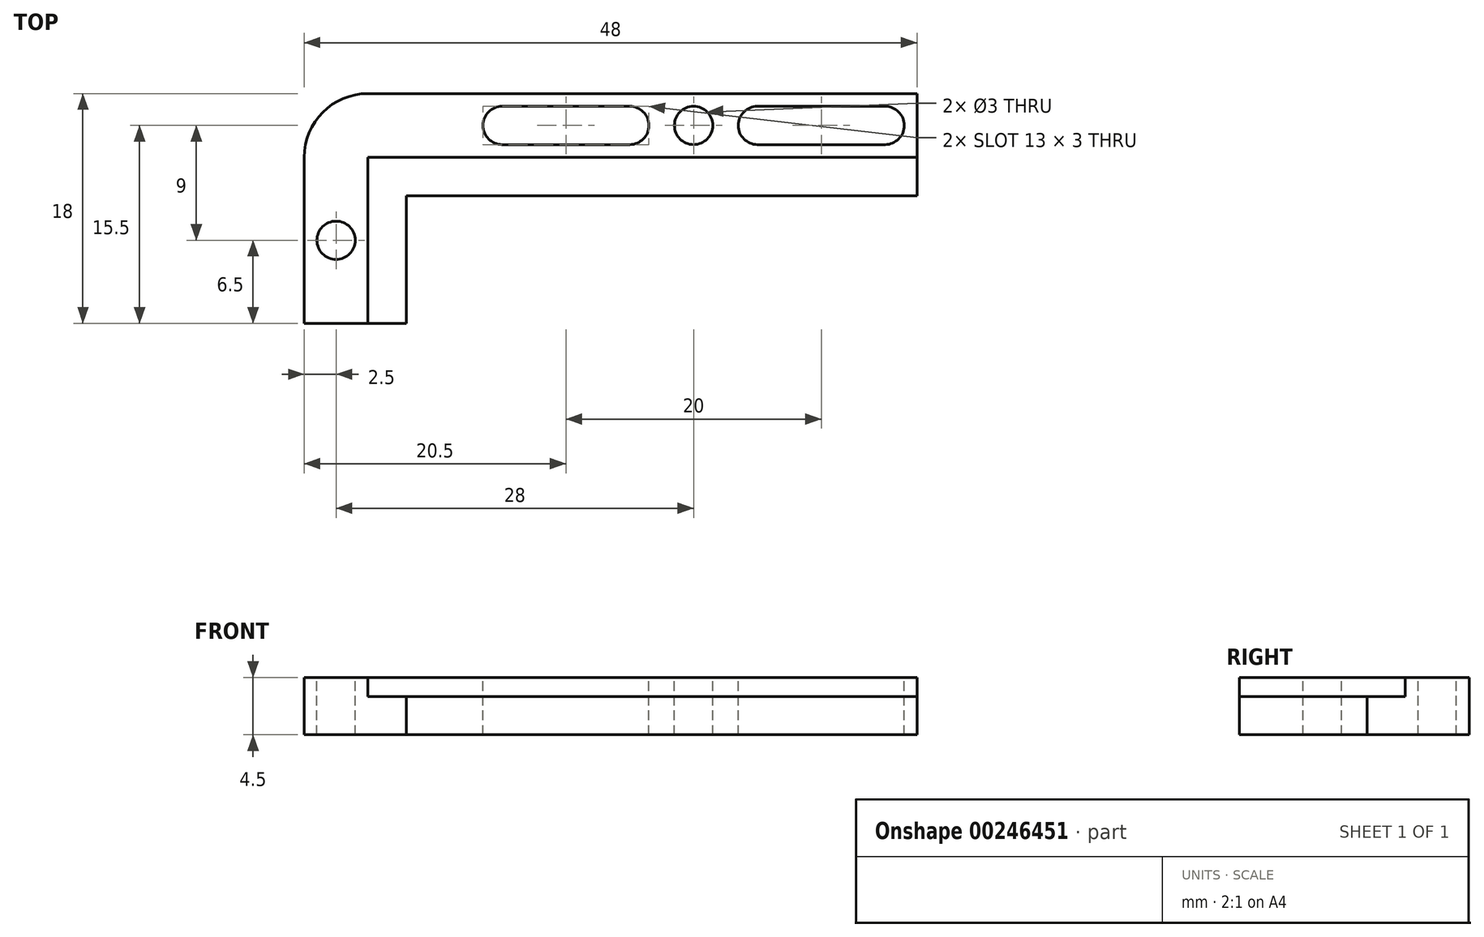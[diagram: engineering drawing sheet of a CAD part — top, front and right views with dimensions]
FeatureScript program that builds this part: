
annotation { "Feature Type Name" : "Feature", "Feature Type Description" : "" }
export const myFeature = defineFeature(function(context is Context, id is Id, definition is map)
    precondition{}
    {
        {
            assignVariable(context, id + "F0", {"name" : "pcb_thickness", "anyValue" : 1.5});
        }
        {
            assignVariable(context, id + "F1", {"name" : "clamp_thickness", "anyValue" : 3});
        }
        {
            assignVariable(context, id + "F2", {"name" : "clamp_depth", "anyValue" : 5});
        }
        {
            var Q0;
            Q0=qCreatedBy(makeId("Top.planeOp"),FACE);
            var sketch = newSketch(context, id + "F3", { "sketchPlane" : qUnion([Q0])});
            skLineSegment(sketch, "E0", {"start": v(0, 0) * mm, "end": v(40, 0) * mm});
            skLineSegment(sketch, "E1", {"start": v(40, 0) * mm, "end": v(40, 8) * mm});
            skLineSegment(sketch, "E2", {"start": v(40, 8) * mm, "end": v(-8, 8) * mm});
            skLineSegment(sketch, "E3", {"start": v(-8, 8) * mm, "end": v(-8, -10) * mm});
            skLineSegment(sketch, "E4", {"start": v(-8, -10) * mm, "end": v(0, -10) * mm});
            skLineSegment(sketch, "E5", {"start": v(0, -10) * mm, "end": v(0, 0) * mm});
            skSolve(sketch);
        }
        {
            var Q0;
            Q0 = qSketchRegion(id + "F3", true);
            extrude(context, id + "F4", {"entities" : qUnion([Q0]), "depth" : (getVariable(context, 'clamp_thickness') + getVariable(context, 'pcb_thickness')) * mm});
        }
        {
            var Q0;
            Q0=makeQuery(id+"F4.opExtrude","SWEPT_FACE",FACE,{"disambiguationData":[OSD([sQuery(id+"F3.wireOp",EDGE,"E1")])]});
            var sketch = newSketch(context, id + "F5", { "sketchPlane" : qUnion([Q0])});
            skLineSegment(sketch, "E6.bottom", {"start": v(0, 4.5) * mm, "end": v(3, 4.5) * mm});
            skLineSegment(sketch, "E6.top", {"start": v(0, 3) * mm, "end": v(3, 3) * mm});
            skLineSegment(sketch, "E6.left", {"start": v(0, 4.5) * mm, "end": v(0, 3) * mm});
            skLineSegment(sketch, "E6.right", {"start": v(3, 4.5) * mm, "end": v(3, 3) * mm});
            skSolve(sketch);
        }
        {
            var Q0;
            Q0=makeQuery(id+"F5.imprint","IMPRINT",FACE,{"disambiguationData":[TD([[makeQuery(id+"F5.imprint","IMPRINT",EDGE,{"derivedFrom":sQuery(id+"F5.wireOp",EDGE,"E6.bottom")}),-1.0]])]});
            var Q1;
            Q1=makeQuery(id+"F4.opExtrude","CAP_EDGE",EDGE,{"disambiguationData":[OSD([sQuery(id+"F3.wireOp",EDGE,"E0")])],"isStart":false});
            var Q2;
            Q2=makeQuery(id+"F4.opExtrude","CAP_EDGE",EDGE,{"disambiguationData":[OSD([sQuery(id+"F3.wireOp",EDGE,"E5")])],"isStart":false});
            sweep(context, id + "F6", {"operationType" : NewBodyOperationType.REMOVE, "profiles" : qUnion([Q0]), "path" : qUnion([Q1, Q2])});
        }
        {
            var Q0;
            Q0=makeQuery(id+"F4.opExtrude","CAP_FACE",FACE,{"disambiguationData":[OSD([sQuery(id+"F3.wireOp",EDGE,"E0"),sQuery(id+"F3.wireOp",EDGE,"E1"),sQuery(id+"F3.wireOp",EDGE,"E2"),sQuery(id+"F3.wireOp",EDGE,"E3"),sQuery(id+"F3.wireOp",EDGE,"E4"),sQuery(id+"F3.wireOp",EDGE,"E5")])],"isStart":false});
            var sketch = newSketch(context, id + "F7", { "sketchPlane" : qUnion([Q0])});
            skArc(sketch, "E7", {"start": v(37.5, 4) * mm, "mid": v(39, 5.5) * mm, "end": v(37.5, 7) * mm});
            skLineSegment(sketch, "E8", {"start": v(40, 5.5) * mm, "end": v(-8, 5.5) * mm, "construction": true});
            skLineSegment(sketch, "E9", {"start": v(-5.5, -10) * mm, "end": v(-5.5, 8) * mm, "construction": true});
            skArc(sketch, "E10", {"start": v(27.5, 7) * mm, "mid": v(26, 5.5) * mm, "end": v(27.5, 4) * mm});
            skLineSegment(sketch, "E11", {"start": v(27.5, 7) * mm, "end": v(37.5, 7) * mm});
            skLineSegment(sketch, "E12", {"start": v(27.5, 4) * mm, "end": v(37.5, 4) * mm});
            skArc(sketch, "E13", {"start": v(17.5, 4) * mm, "mid": v(19, 5.5) * mm, "end": v(17.5, 7) * mm});
            skArc(sketch, "E14", {"start": v(7.5, 7) * mm, "mid": v(6, 5.5) * mm, "end": v(7.5, 4) * mm});
            skLineSegment(sketch, "E15", {"start": v(7.5, 7) * mm, "end": v(17.5, 7) * mm});
            skLineSegment(sketch, "E16", {"start": v(7.5, 4) * mm, "end": v(17.5, 4) * mm});
            skLineSegment(sketch, "E17", {"start": v(-3, -3.5) * mm, "end": v(-8, -3.5) * mm, "construction": true});
            skCircle(sketch, "E18", {"center": v(-5.5, -3.5) * mm, "radius": 1.5 * mm});
            skCircle(sketch, "E19", {"center": v(22.5, 5.5) * mm, "radius": 1.5 * mm});
            skSolve(sketch);
        }
        {
            var Q0;
            Q0=makeQuery(id+"F7.imprint","IMPRINT",FACE,{"disambiguationData":[TD([[makeQuery(id+"F7.imprint","IMPRINT",EDGE,{"derivedFrom":sQuery(id+"F7.wireOp",EDGE,"E18")}),1.0]])]});
            var Q1;
            Q1=makeQuery(id+"F7.imprint","IMPRINT",FACE,{"disambiguationData":[TD([[makeQuery(id+"F7.imprint","IMPRINT",EDGE,{"derivedFrom":sQuery(id+"F7.wireOp",EDGE,"E13")}),1.0]])]});
            var Q2;
            Q2=makeQuery(id+"F7.imprint","IMPRINT",FACE,{"disambiguationData":[TD([[makeQuery(id+"F7.imprint","IMPRINT",EDGE,{"derivedFrom":sQuery(id+"F7.wireOp",EDGE,"E19")}),1.0]])]});
            var Q3;
            Q3=makeQuery(id+"F7.imprint","IMPRINT",FACE,{"disambiguationData":[TD([[makeQuery(id+"F7.imprint","IMPRINT",EDGE,{"derivedFrom":sQuery(id+"F7.wireOp",EDGE,"E7")}),1.0]])]});
            extrude(context, id + "F8", {"entities" : qUnion([Q0, Q1, Q2, Q3]), "operationType" : NewBodyOperationType.REMOVE, "endBound" : BoundingType.UP_TO_NEXT, "oppositeDirection" : true, "depth" : 25 * mm});
        }
        {
            var Q0;
            Q0=makeQuery(id+"F4.opExtrude","SWEPT_EDGE",EDGE,{"disambiguationData":[OSD([sQuery(id+"F3.wireOp",EDGE,"E2"),sQuery(id+"F3.wireOp",EDGE,"E3")])]});
            fillet(context, id + "F9", {"entities" : qUnion([Q0]), "radius" : (getVariable(context, 'clamp_depth')) * mm, "tangentPropagation" : true, "allowEdgeOverflow" : false});
        }
    });
